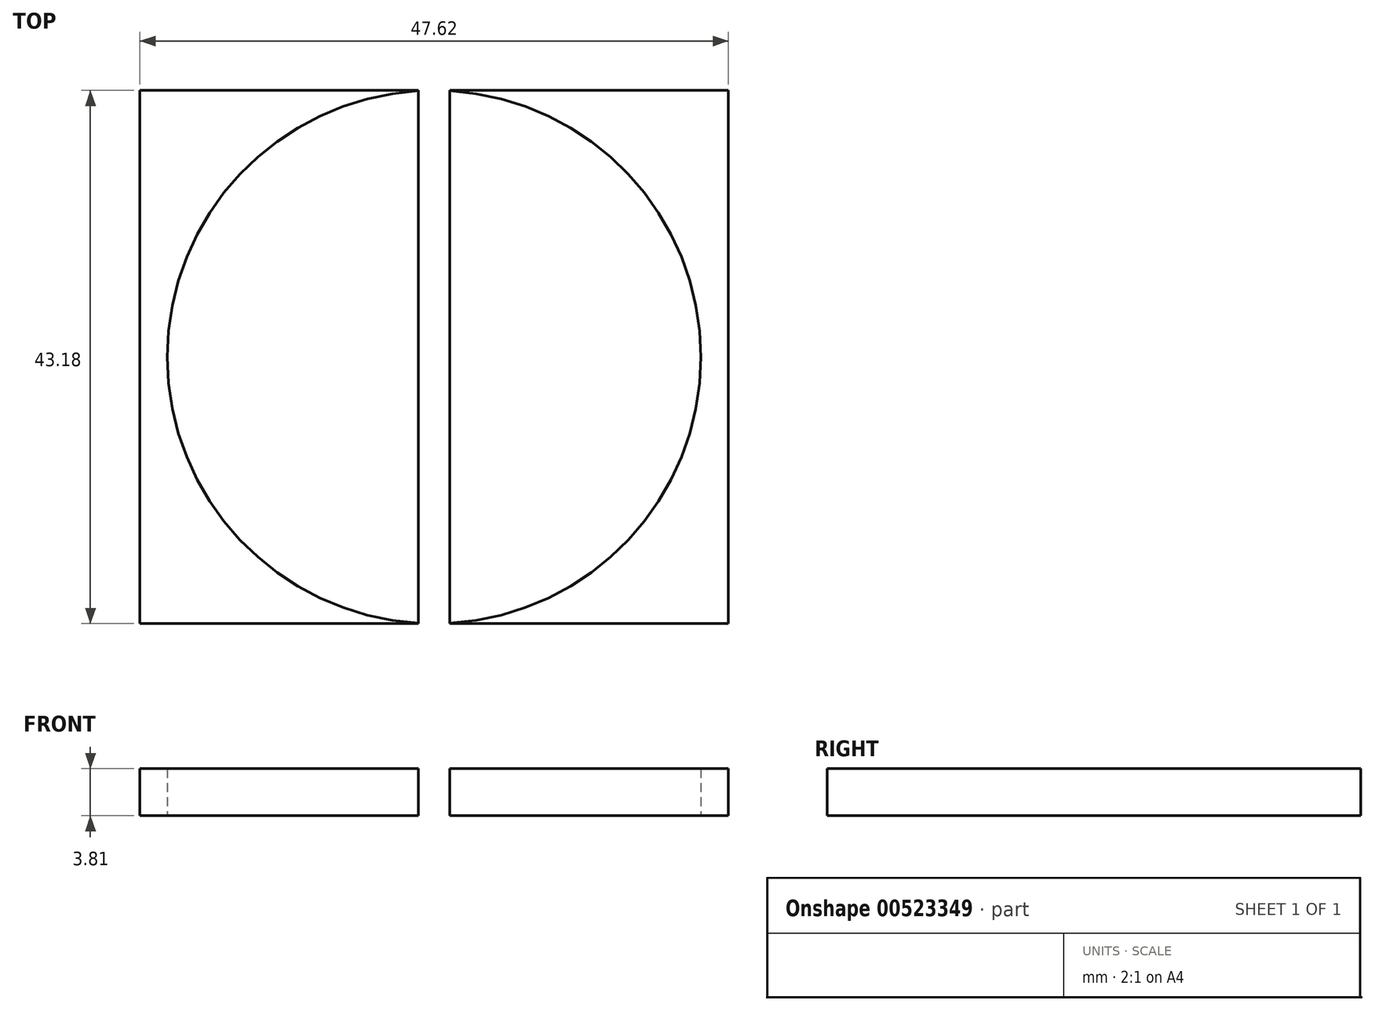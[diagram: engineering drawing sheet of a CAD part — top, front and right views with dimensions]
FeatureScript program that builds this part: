
annotation { "Feature Type Name" : "Feature", "Feature Type Description" : "" }
export const myFeature = defineFeature(function(context is Context, id is Id, definition is map)
    precondition{}
    {
        {
            var Q0;
            Q0=qCreatedBy(makeId("Top.planeOp"),FACE);
            var sketch = newSketch(context, id + "F0", { "sketchPlane" : qUnion([Q0])});
            skCircle(sketch, "E0", {"center": v(0, 0) * mm, "radius": 21.59 * mm});
            skSolve(sketch);
        }
        {
            var Q0;
            Q0 = qSketchRegion(id + "F0", true);
            extrude(context, id + "F1", {"entities" : qUnion([Q0]), "depth" : 3.8 * mm, "offsetDistance" : 25.4 * mm});
        }
        {
            var Q0;
            {var subQ0=sQuery(id+"F0.wireOp",EDGE,"E0");Q0=makeQuery(id+"FDrLIAqkUXGuBmI_1.boolean.opBoolean","SPLIT",FACE,{"disambiguationData":[TD([makeQuery(id+"FDrLIAqkUXGuBmI_1.opExtrude","SWEPT_FACE",FACE,{"disambiguationData":[OSD([sQuery(id+"FfFdZmhNwIpX2hx_1.wireOp",EDGE,"LWKYM41H-w1TK-FHdA-1j9n-13W1JXHBk9NG.left")])]})])],"derivedFrom":makeQuery(id+"F1.opExtrude","CAP_FACE",FACE,{"disambiguationData":[OSD([subQ0])],"isStart":true})});}
            var sketch = newSketch(context, id + "F2", { "sketchPlane" : qUnion([Q0])});
            skLineSegment(sketch, "E1.bottom", {"start": v(-23.8, 21.59) * mm, "end": v(23.8, 21.59) * mm});
            skLineSegment(sketch, "E1.top", {"start": v(-23.8, -21.59) * mm, "end": v(23.8, -21.59) * mm});
            skLineSegment(sketch, "E1.left", {"start": v(-23.8, 21.59) * mm, "end": v(-23.8, -21.59) * mm});
            skLineSegment(sketch, "E1.right", {"start": v(23.8, 21.59) * mm, "end": v(23.8, -21.59) * mm});
            skSolve(sketch);
        }
        {
            var Q0;
            Q0 = qSketchRegion(id + "F2", true);
            extrude(context, id + "F3", {"entities" : qUnion([Q0]), "oppositeDirection" : true, "depth" : 3.8 * mm, "offsetDistance" : 25.4 * mm});
        }
        {
            var Q0;
            Q0=qCreatedBy(makeId("Top.planeOp"),FACE);
            var sketch = newSketch(context, id + "F4", { "sketchPlane" : qUnion([Q0])});
            skLineSegment(sketch, "E2.bottom", {"start": v(-1.27, -22.87) * mm, "end": v(1.27, -22.87) * mm});
            skLineSegment(sketch, "E2.top", {"start": v(-1.27, 22.87) * mm, "end": v(1.27, 22.87) * mm});
            skLineSegment(sketch, "E2.left", {"start": v(-1.27, -22.87) * mm, "end": v(-1.27, 22.87) * mm});
            skLineSegment(sketch, "E2.right", {"start": v(1.27, -22.87) * mm, "end": v(1.27, 22.87) * mm});
            skSolve(sketch);
        }
        {
            var Q0;
            Q0 = qSketchRegion(id + "F4", true);
            extrude(context, id + "F5", {"entities" : qUnion([Q0]), "operationType" : NewBodyOperationType.REMOVE, "depth" : 4.06 * mm, "offsetDistance" : 25.4 * mm});
        }
    });
